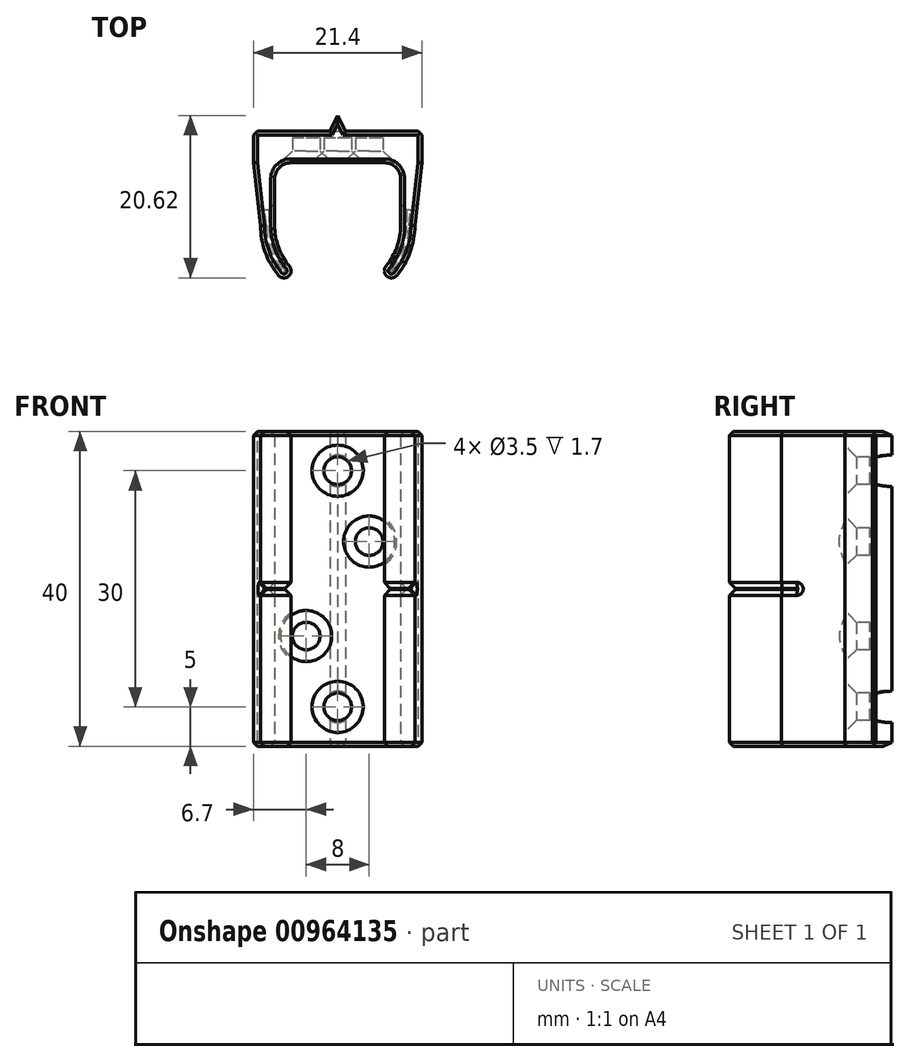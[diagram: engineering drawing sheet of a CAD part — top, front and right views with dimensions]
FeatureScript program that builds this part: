
annotation { "Feature Type Name" : "Feature", "Feature Type Description" : "" }
export const myFeature = defineFeature(function(context is Context, id is Id, definition is map)
    precondition{}
    {
        {
            var Q0;
            Q0=qCreatedBy(makeId("Top.planeOp"),FACE);
            var sketch = newSketch(context, id + "F0", { "sketchPlane" : qUnion([Q0])});
            skLineSegment(sketch, "E0", {"start": v(-10.7, 12) * mm, "end": v(-1, 12) * mm});
            skLineSegment(sketch, "E1", {"start": v(10.7, 12) * mm, "end": v(10.7, 8) * mm});
            skLineSegment(sketch, "E2", {"start": v(-10.7, 12) * mm, "end": v(-10.7, 8) * mm});
            skLineSegment(sketch, "E3", {"start": v(-1, 12) * mm, "end": v(0, 14) * mm});
            skLineSegment(sketch, "E4", {"start": v(0, 14) * mm, "end": v(1, 12) * mm});
            skLineSegment(sketch, "E5.trimOffspring", {"start": v(1, 12) * mm, "end": v(10.7, 12) * mm});
            skLineSegment(sketch, "E6", {"start": v(-8.05, -0.92) * mm, "end": v(-8.05, -0.92) * mm});
            skPoint(sketch, "E7.visualSharp", {"position": v(-10.7, 12) * mm});
            skPoint(sketch, "E8.visualSharp", {"position": v(10.7, 12) * mm});
            skLineSegment(sketch, "E9", {"start": v(0, 0) * mm, "end": v(-19.15, -16.07) * mm, "construction": true});
            skLineSegment(sketch, "E10", {"start": v(0, 0) * mm, "end": v(19.15, -16.07) * mm, "construction": true});
            skLineSegment(sketch, "E11", {"start": v(0, 0) * mm, "end": v(0, -25) * mm, "construction": true});
            skArc(sketch, "E12", {"start": v(6.13, -5.14) * mm, "mid": v(7.52, -2.74) * mm, "end": v(8, 0) * mm});
            skArc(sketch, "E13", {"start": v(-9.8, 0) * mm, "mid": v(-9.2, -3.35) * mm, "end": v(-7.5, -6.3) * mm});
            skLineSegment(sketch, "E14", {"start": v(-10.7, 8) * mm, "end": v(-9.8, 0) * mm});
            skLineSegment(sketch, "E15", {"start": v(10.7, 8) * mm, "end": v(9.8, 0) * mm});
            skArc(sketch, "E16.trimOffspring", {"start": v(7.5, -6.3) * mm, "mid": v(9.2, -3.35) * mm, "end": v(9.8, 0) * mm});
            skArc(sketch, "E17", {"start": v(-6.13, -5.14) * mm, "mid": v(-6.24, -6.41) * mm, "end": v(-7.5, -6.3) * mm});
            skArc(sketch, "E18", {"start": v(6.13, -5.14) * mm, "mid": v(6.24, -6.41) * mm, "end": v(7.5, -6.3) * mm});
            skLineSegment(sketch, "E19", {"start": v(-8, 0) * mm, "end": v(-8, 6) * mm});
            skLineSegment(sketch, "E20", {"start": v(8, 0) * mm, "end": v(8, 6) * mm});
            skLineSegment(sketch, "E21", {"start": v(-6, 8) * mm, "end": v(6, 8) * mm});
            skArc(sketch, "E22.trimOffspring", {"start": v(-8, 0) * mm, "mid": v(-7.52, -2.74) * mm, "end": v(-6.13, -5.14) * mm});
            skPoint(sketch, "E23.visualSharp", {"position": v(-8, 8) * mm});
            skArc(sketch, "E23.filletArc", {"start": v(-6, 8) * mm, "mid": v(-7.41, 7.41) * mm, "end": v(-8, 6) * mm});
            skPoint(sketch, "E24.visualSharp", {"position": v(8, 8) * mm});
            skArc(sketch, "E24.filletArc", {"start": v(8, 6) * mm, "mid": v(7.41, 7.41) * mm, "end": v(6, 8) * mm});
            skSolve(sketch);
        }
        {
            var Q0;
            Q0=qSketchRegion(id+"F0",true);
            extrude(context, id + "F1", {"entities" : qUnion([Q0]), "endBound" : BoundingType.SYMMETRIC, "depth" : 40 * mm, "offsetDistance" : 25 * mm});
        }
        {
            var Q0;
            Q0=qCreatedBy(makeId("Front.planeOp"),FACE);
            cPlane(context, id + "F2", {"entities" : qUnion([Q0]), "cplaneType" : CPlaneType.OFFSET, "offset" : 12 * mm, "oppositeDirection" : true, "width" : 150 * mm, "height" : 150 * mm});
        }
        {
            var Q0;
            Q0=qCreatedBy(makeId("Front.planeOp"),FACE);
            var sketch = newSketch(context, id + "F3", { "sketchPlane" : qUnion([Q0])});
            skCircle(sketch, "E25", {"center": v(0, 15) * mm, "radius": 1.75 * mm});
            skCircle(sketch, "E26", {"center": v(0, -15) * mm, "radius": 1.75 * mm});
            skCircle(sketch, "E27", {"center": v(4, 6) * mm, "radius": 1.75 * mm});
            skCircle(sketch, "E28", {"center": v(-4, -6) * mm, "radius": 1.75 * mm});
            skSolve(sketch);
        }
        {
            var Q0;
            Q0=qSketchRegion(id+"F3",true);
            extrude(context, id + "F4", {"entities" : qUnion([Q0]), "operationType" : NewBodyOperationType.REMOVE, "oppositeDirection" : true, "depth" : 11.2 * mm, "offsetDistance" : 25 * mm});
        }
        {
            var Q0;
            Q0=qCreatedBy(makeId("Front.planeOp"),FACE);
            var sketch = newSketch(context, id + "F5", { "sketchPlane" : qUnion([Q0])});
            skCircle(sketch, "E29", {"center": v(0, 15) * mm, "radius": 3.5 * mm});
            skCircle(sketch, "E30", {"center": v(4, 6) * mm, "radius": 3.5 * mm});
            skCircle(sketch, "E31", {"center": v(-4, -6) * mm, "radius": 3.5 * mm});
            skCircle(sketch, "E32", {"center": v(0, -15) * mm, "radius": 3.5 * mm});
            skSolve(sketch);
        }
        {
            var Q0;
            Q0=qSketchRegion(id+"F5",true);
            extrude(context, id + "F6", {"entities" : qUnion([Q0]), "operationType" : NewBodyOperationType.REMOVE, "oppositeDirection" : true, "depth" : 8 * mm, "offsetDistance" : 25 * mm});
        }
        {
            var Q0;
            Q0=makeQuery(id+"F4.boolean.opBoolean","INTERSECT",EDGE,{"derivedFrom":[makeQuery(id+"F1.opExtrude","SWEPT_FACE",FACE,{"disambiguationData":[OSD([sQuery(id+"F0.wireOp",EDGE,"E21")])]}),makeQuery(id+"F4.opExtrude","SWEPT_FACE",FACE,{"disambiguationData":[OSD([sQuery(id+"F3.wireOp",EDGE,"E26")])]})]});
            var Q1;
            Q1=makeQuery(id+"F4.boolean.opBoolean","INTERSECT",EDGE,{"derivedFrom":[makeQuery(id+"F1.opExtrude","SWEPT_FACE",FACE,{"disambiguationData":[OSD([sQuery(id+"F0.wireOp",EDGE,"E21")])]}),makeQuery(id+"F4.opExtrude","SWEPT_FACE",FACE,{"disambiguationData":[OSD([sQuery(id+"F3.wireOp",EDGE,"E28")])]})]});
            var Q2;
            Q2=makeQuery(id+"F4.boolean.opBoolean","INTERSECT",EDGE,{"derivedFrom":[makeQuery(id+"F1.opExtrude","SWEPT_FACE",FACE,{"disambiguationData":[OSD([sQuery(id+"F0.wireOp",EDGE,"E21")])]}),makeQuery(id+"F4.opExtrude","SWEPT_FACE",FACE,{"disambiguationData":[OSD([sQuery(id+"F3.wireOp",EDGE,"E25")])]})]});
            var Q3;
            Q3=makeQuery(id+"F4.boolean.opBoolean","INTERSECT",EDGE,{"derivedFrom":[makeQuery(id+"F1.opExtrude","SWEPT_FACE",FACE,{"disambiguationData":[OSD([sQuery(id+"F0.wireOp",EDGE,"E21")])]}),makeQuery(id+"F4.opExtrude","SWEPT_FACE",FACE,{"disambiguationData":[OSD([sQuery(id+"F3.wireOp",EDGE,"E27")])]})]});
            chamfer(context, id + "F7", {"entities" : qUnion([Q0, Q1, Q2, Q3]), "width" : 1.5 * mm, "tangentPropagation" : true});
        }
        {
            var Q0;
            Q0=makeQuery(id+"F1.opExtrude","CAP_EDGE",EDGE,{"disambiguationData":[OSD([sQuery(id+"F0.wireOp",EDGE,"E13")])],"isStart":true});
            var Q1;
            Q1=makeQuery(id+"F1.opExtrude","CAP_EDGE",EDGE,{"disambiguationData":[OSD([sQuery(id+"F0.wireOp",EDGE,"E12")])],"isStart":true});
            var Q2;
            Q2=makeQuery(id+"F1.opExtrude","CAP_EDGE",EDGE,{"disambiguationData":[OSD([sQuery(id+"F0.wireOp",EDGE,"E14")])],"isStart":true});
            var Q3;
            Q3=makeQuery(id+"F1.opExtrude","CAP_EDGE",EDGE,{"disambiguationData":[OSD([sQuery(id+"F0.wireOp",EDGE,"E0")])],"isStart":true});
            var Q4;
            Q4=makeQuery(id+"F1.opExtrude","CAP_EDGE",EDGE,{"disambiguationData":[OSD([sQuery(id+"F0.wireOp",EDGE,"E5.trimOffspring")])],"isStart":true});
            var Q5;
            Q5=makeQuery(id+"F1.opExtrude","CAP_EDGE",EDGE,{"disambiguationData":[OSD([sQuery(id+"F0.wireOp",EDGE,"E4")])],"isStart":true});
            var Q6;
            Q6=makeQuery(id+"F1.opExtrude","CAP_EDGE",EDGE,{"disambiguationData":[OSD([sQuery(id+"F0.wireOp",EDGE,"E3")])],"isStart":true});
            var Q7;
            Q7=makeQuery(id+"F1.opExtrude","CAP_EDGE",EDGE,{"disambiguationData":[OSD([sQuery(id+"F0.wireOp",EDGE,"E2")])],"isStart":true});
            var Q8;
            Q8=makeQuery(id+"F1.opExtrude","CAP_EDGE",EDGE,{"disambiguationData":[OSD([sQuery(id+"F0.wireOp",EDGE,"E17")])],"isStart":true});
            var Q9;
            Q9=makeQuery(id+"F1.opExtrude","CAP_EDGE",EDGE,{"disambiguationData":[OSD([sQuery(id+"F0.wireOp",EDGE,"E18")])],"isStart":true});
            var Q10;
            Q10=makeQuery(id+"F1.opExtrude","CAP_EDGE",EDGE,{"disambiguationData":[OSD([sQuery(id+"F0.wireOp",EDGE,"E16.trimOffspring")])],"isStart":true});
            var Q11;
            Q11=makeQuery(id+"F1.opExtrude","CAP_EDGE",EDGE,{"disambiguationData":[OSD([sQuery(id+"F0.wireOp",EDGE,"E15")])],"isStart":true});
            var Q12;
            Q12=makeQuery(id+"F1.opExtrude","CAP_EDGE",EDGE,{"disambiguationData":[OSD([sQuery(id+"F0.wireOp",EDGE,"E1")])],"isStart":true});
            var Q13;
            Q13=makeQuery(id+"F1.opExtrude","CAP_FACE",FACE,{"disambiguationData":[OSD([sQuery(id+"F0.wireOp",EDGE,"E0"),sQuery(id+"F0.wireOp",EDGE,"E1"),sQuery(id+"F0.wireOp",EDGE,"E2"),sQuery(id+"F0.wireOp",EDGE,"E3"),sQuery(id+"F0.wireOp",EDGE,"E4"),sQuery(id+"F0.wireOp",EDGE,"E5.trimOffspring"),sQuery(id+"F0.wireOp",EDGE,"E12"),sQuery(id+"F0.wireOp",EDGE,"E13"),sQuery(id+"F0.wireOp",EDGE,"E14"),sQuery(id+"F0.wireOp",EDGE,"E15"),sQuery(id+"F0.wireOp",EDGE,"E16.trimOffspring"),sQuery(id+"F0.wireOp",EDGE,"E17"),sQuery(id+"F0.wireOp",EDGE,"E18")])],"isStart":false});
            chamfer(context, id + "F8", {"entities" : qUnion([Q0, Q1, Q2, Q3, Q4, Q5, Q6, Q7, Q8, Q9, Q10, Q11, Q12, Q13]), "width" : .5 * mm, "tangentPropagation" : true});
        }
        {
            var Q0;
            Q0=makeQuery(id+"F1.opExtrude","SWEPT_EDGE",EDGE,{"disambiguationData":[OSD([sQuery(id+"F0.wireOp",EDGE,"E1"),sQuery(id+"F0.wireOp",EDGE,"E5.trimOffspring")])]});
            var Q1;
            Q1=makeQuery(id+"F1.opExtrude","SWEPT_EDGE",EDGE,{"disambiguationData":[OSD([sQuery(id+"F0.wireOp",EDGE,"E0"),sQuery(id+"F0.wireOp",EDGE,"E2")])]});
            chamfer(context, id + "F9", {"entities" : qUnion([Q0, Q1]), "width" : .5 * mm, "tangentPropagation" : true});
        }
        {
            var Q0;
            Q0=qCreatedBy(id+"F2.planeOp",FACE);
            var sketch = newSketch(context, id + "F10", { "sketchPlane" : qUnion([Q0])});
            skCircle(sketch, "E33", {"center": v(0, 15) * mm, "radius": 2 * mm});
            skCircle(sketch, "E34", {"center": v(0, -15) * mm, "radius": 2 * mm});
            skCircle(sketch, "E35", {"center": v(4, 6) * mm, "radius": 2 * mm});
            skCircle(sketch, "E36", {"center": v(-4, -6) * mm, "radius": 2 * mm});
            skSolve(sketch);
        }
        {
            var Q0;
            Q0=qSketchRegion(id+"F10",true);
            extrude(context, id + "F11", {"entities" : qUnion([Q0]), "operationType" : NewBodyOperationType.REMOVE, "oppositeDirection" : true, "depth" : 2 * mm, "offsetDistance" : 25 * mm});
        }
        {
            var Q0;
            Q0=qCreatedBy(makeId("Right.planeOp"),FACE);
            var sketch = newSketch(context, id + "F12", { "sketchPlane" : qUnion([Q0])});
            skLineSegment(sketch, "E37.bottom", {"start": v(-8, 0.07) * mm, "end": v(2, 0.07) * mm});
            skLineSegment(sketch, "E37.top", {"start": v(-8, -0.07) * mm, "end": v(2, -0.07) * mm});
            skLineSegment(sketch, "E37.left", {"start": v(-8, 0.07) * mm, "end": v(-8, -0.07) * mm});
            skArc(sketch, "E38", {"start": v(2, 0.07) * mm, "mid": v(2.08, 0) * mm, "end": v(2, -0.08) * mm});
            skSolve(sketch);
        }
        {
            var Q0;
            Q0 = qSketchRegion(id + "F12", true);
            extrude(context, id + "F13", {"entities" : qUnion([Q0]), "operationType" : NewBodyOperationType.REMOVE, "endBound" : BoundingType.SYMMETRIC, "oppositeDirection" : true, "depth" : 25 * mm, "offsetDistance" : 25 * mm});
        }
        {
            var Q0;
            Q0=makeQuery(id+"F13.boolean.opBoolean","INTERSECT",EDGE,{"derivedFrom":[makeQuery(id+"F1.opExtrude","SWEPT_FACE",FACE,{"disambiguationData":[OSD([sQuery(id+"F0.wireOp",EDGE,"E16.trimOffspring")])]}),makeQuery(id+"F13.opExtrude","SWEPT_FACE",FACE,{"disambiguationData":[OSD([sQuery(id+"F12.wireOp",EDGE,"E37.top")])]})]});
            var Q1;
            Q1=makeQuery(id+"F13.boolean.opBoolean","INTERSECT",EDGE,{"derivedFrom":[makeQuery(id+"F1.opExtrude","SWEPT_FACE",FACE,{"disambiguationData":[OSD([sQuery(id+"F0.wireOp",EDGE,"E16.trimOffspring")])]}),makeQuery(id+"F13.opExtrude","SWEPT_FACE",FACE,{"disambiguationData":[OSD([sQuery(id+"F12.wireOp",EDGE,"E37.bottom")])]})]});
            var Q2;
            Q2=makeQuery(id+"F13.boolean.opBoolean","INTERSECT",EDGE,{"derivedFrom":[makeQuery(id+"F1.opExtrude","SWEPT_FACE",FACE,{"disambiguationData":[OSD([sQuery(id+"F0.wireOp",EDGE,"E15")])]}),makeQuery(id+"F13.opExtrude","SWEPT_FACE",FACE,{"disambiguationData":[OSD([sQuery(id+"F12.wireOp",EDGE,"E37.bottom")])]})]});
            var Q3;
            Q3=makeQuery(id+"F13.boolean.opBoolean","INTERSECT",EDGE,{"derivedFrom":[makeQuery(id+"F1.opExtrude","SWEPT_FACE",FACE,{"disambiguationData":[OSD([sQuery(id+"F0.wireOp",EDGE,"E15")])]}),makeQuery(id+"F13.opExtrude","SWEPT_FACE",FACE,{"disambiguationData":[OSD([sQuery(id+"F12.wireOp",EDGE,"E37.top")])]})]});
            var Q4;
            Q4=makeQuery(id+"F13.boolean.opBoolean","INTERSECT",EDGE,{"derivedFrom":[makeQuery(id+"F1.opExtrude","SWEPT_FACE",FACE,{"disambiguationData":[OSD([sQuery(id+"F0.wireOp",EDGE,"E22.trimOffspring")])]}),makeQuery(id+"F13.opExtrude","SWEPT_FACE",FACE,{"disambiguationData":[OSD([sQuery(id+"F12.wireOp",EDGE,"E37.top")])]})]});
            var Q5;
            Q5=makeQuery(id+"F13.boolean.opBoolean","INTERSECT",EDGE,{"derivedFrom":[makeQuery(id+"F1.opExtrude","SWEPT_FACE",FACE,{"disambiguationData":[OSD([sQuery(id+"F0.wireOp",EDGE,"E22.trimOffspring")])]}),makeQuery(id+"F13.opExtrude","SWEPT_FACE",FACE,{"disambiguationData":[OSD([sQuery(id+"F12.wireOp",EDGE,"E37.bottom")])]})]});
            var Q6;
            Q6=makeQuery(id+"F13.boolean.opBoolean","INTERSECT",EDGE,{"derivedFrom":[makeQuery(id+"F1.opExtrude","SWEPT_FACE",FACE,{"disambiguationData":[OSD([sQuery(id+"F0.wireOp",EDGE,"E19")])]}),makeQuery(id+"F13.opExtrude","SWEPT_FACE",FACE,{"disambiguationData":[OSD([sQuery(id+"F12.wireOp",EDGE,"E37.bottom")])]})]});
            var Q7;
            Q7=makeQuery(id+"F13.boolean.opBoolean","INTERSECT",EDGE,{"derivedFrom":[makeQuery(id+"F1.opExtrude","SWEPT_FACE",FACE,{"disambiguationData":[OSD([sQuery(id+"F0.wireOp",EDGE,"E19")])]}),makeQuery(id+"F13.opExtrude","SWEPT_FACE",FACE,{"disambiguationData":[OSD([sQuery(id+"F12.wireOp",EDGE,"E37.top")])]})]});
            var Q8;
            Q8=makeQuery(id+"F13.boolean.opBoolean","INTERSECT",EDGE,{"derivedFrom":[makeQuery(id+"F1.opExtrude","SWEPT_FACE",FACE,{"disambiguationData":[OSD([sQuery(id+"F0.wireOp",EDGE,"E19")])]}),makeQuery(id+"F13.opExtrude","SWEPT_FACE",FACE,{"disambiguationData":[OSD([sQuery(id+"F12.wireOp",EDGE,"E38")])]})]});
            var Q9;
            Q9=makeQuery(id+"F13.boolean.opBoolean","INTERSECT",EDGE,{"derivedFrom":[makeQuery(id+"F1.opExtrude","SWEPT_FACE",FACE,{"disambiguationData":[OSD([sQuery(id+"F0.wireOp",EDGE,"E14")])]}),makeQuery(id+"F13.opExtrude","SWEPT_FACE",FACE,{"disambiguationData":[OSD([sQuery(id+"F12.wireOp",EDGE,"E38")])]})]});
            var Q10;
            Q10=makeQuery(id+"F13.boolean.opBoolean","INTERSECT",EDGE,{"derivedFrom":[makeQuery(id+"F1.opExtrude","SWEPT_FACE",FACE,{"disambiguationData":[OSD([sQuery(id+"F0.wireOp",EDGE,"E14")])]}),makeQuery(id+"F13.opExtrude","SWEPT_FACE",FACE,{"disambiguationData":[OSD([sQuery(id+"F12.wireOp",EDGE,"E37.bottom")])]})]});
            chamfer(context, id + "F14", {"entities" : qUnion([Q0, Q1, Q2, Q3, Q4, Q5, Q6, Q7, Q8, Q9, Q10]), "width" : .75 * mm, "tangentPropagation" : true});
        }
    });
